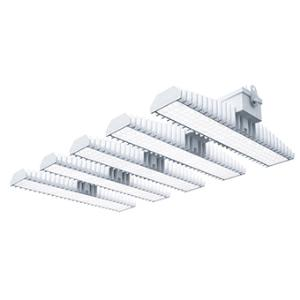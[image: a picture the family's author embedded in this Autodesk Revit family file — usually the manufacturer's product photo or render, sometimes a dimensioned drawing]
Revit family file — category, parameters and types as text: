
# Revit family: 3f_filippi_-_3f_lem_ht_ampio_3f_filippi_-_59030_a0812_-_3f_lem_5_ht_led_150_cr_ampio___vs_0ec2
name_source: partatom
category: Lighting Fixtures
units: mm (PartAtom-declared; Revit-internal decimal feet)

## family parameters
Cut with Voids When Loaded = No
Host = Face
Light Source = No
Part Type = Normal
Room Calculation Point = No
Round Connector Dimension = Use Diameter
Shared = No

## types (1)
- 3F Filippi - 3F LEM HT Ampio (1 x LED, 21295 lm, 170 W, 4000 K)
    Apparent Load = 170 VA
    Approval mark = ENEC
    CIE Flux Codes = 67 90 97 100 100
    Color Rendering = 80
    Color Temperature = 4000 K
    Control Gear = Electronic ballast
    Default Elevation = 1800 mm
    Description = Industrial luminaire with high light output and high luminous efficiency designed with the most innovative technologies for environments with temperature up to 70°C.

ILLUMINOTECHNICAL
Luminous efficiency 100% (DLOR 98%, ULOR 2%).
Initial luminous flux of the luminaire 21295 lm.
Direct symmetric wide distribution: the illuminated area has a rectangular shape.
Installation Interdistance Transv.D = 1.24 x hu - Long.D = 1.20 x hu.
Tabular UGR (CIE 117 - 4H-8H; S=0.25H; 70/50/20): RUG 21.3 - 21.3.
Beam angle: 82° - 83°.
Luminous efficacy 125 lm/W.
Lifetime (L93/B10): 30000 h. (tq+25°C)
Lifetime (L90/B10): 50000 h. (tq+25°C)
Lifetime (L85/B10): 80000 h. (tq+25°C)
Lifetime (L80/B10): 100000 h. (tq+25°C)
Lifetime (L85/B10): 50000 h. (tq+70°C)
Sudden decreased luminous flux after 50000 hours: 0% (C0).
Photobiological safety in compliance with IEC/TR 62778: RG0 risk exempt, (IEC 62471).
In compliance with IEC/EN 62722-2-1 - IEC/EN 62717 standards.
Luminous flux at +70°C: -13.5%.

SOURCE
5 Mid-Power linear LED modules 30W/840.
Energy efficiency class (UE 2019/2020 - UE 2019/2015): C.
CIE 13.3 Colour rendering index: CRI >80 (R9 <50%).
IES TM-30 Fidelity Index: Rf = 84 Rg = 95.
CCT nominal colour temperature 4000 K.
Colour initial tolerance (MacAdam): SDCM 3.

MECHANICAL
Passive modular heatsinks in die-casted aluminium, painted in white colour.
To optimize the thermal management of the LED module, the heatsinks are oversized and provided with self-cleaning of cooling fins.
Wiring body in aluminium and galvanised steel anchored solidly to the sinks and thermally separated.
3F Lens lenses with high luminous efficiency, transparent polycarbonate, fixed to the LED modules.
Fixing brackets in stainless steel.
Luminaire with limited surface temperature. - D - (EN 60598-2-24)
Dimensions: 952x542 mm, height 133 mm. Weight 23.78 kg.
IP65 protection degree.
Mechanical strength to impacts IK08 (5 joule).
Glow-wire test resistance 850°C.

ELECTRICAL
Halogen Free electronic wiring 230V-50/60Hz, power factor 0.95, THD <25%, constant output current, class I, 2 driver.
Power of the luminaire 170 W.
CE - IEC 60598-1 - EN 60598-1.
SAFE FLICKER: PstLM=<1 and SVM=<0.4 (IEC TR 61547-1 and IEC TR 63158), to ensure a more comfortable and safe light.
Luminaire compliant with EN 60598-2-22 for power supply from a centralised emergency system CPSS (Central Power Supply System), not incorporated in the luminaire - high risk areas excluded. The default power and flux are 100% in AC and 100% in DC.
Ambient temperature from -30°C to +70°C.
Temperature class T6 max 85°C.
Quick connection via M20 3P connector with 9-13 mm tightening range.
Power unit positioned on a separate compartment by the LED module to ensure optimum temperatures of cabling components, to be inspectable and maintainable.
Relative humidity UR: <85%.

INSTALLATION
Ceiling / Suspended / Wall.
All accessories dedicated to this product are available on the Catalog and on our website www.3F-Filippi.com.

ACCESSORIES
A0812 - Anti-glare microprismatic VS moulded glass, tempered, not flammable, with sealing gasket.
One required for each light module. The pack contains 10 pieces.

APPLICATIONS
In commercial environments, exhibition and industrial areas, stores, open areas.
Applications with high ambient temperature up to 70°C.

WARNING
Fixture not suitable for cold stores with an ambient temperature <0°C and/or relative humidity >85%.
Luminaire designed for disposal/recycling at end-of-life.
Replaceable (LED only) light source by a professional. Replaceable control gear by a professional.
    Height = 133 mm  [stored 0.436352 ft]
    Lamp = 1 x LED
    Lamp Light Flux = 21295 lm
    Lamp Power = 170 W
    Lamp count = 1
    Length = 952 mm
    Lifetime = 50000 h
    Luminous efficacy = 125 lm/W
    Manufacturer = 3F Filippi
    ModVariant = No
    Model = 3F Filippi - 59030+A0812 - 3F LEM 5 HT LED 150 CR AMPIO + VS
    Mounting Place = Ceiling
    Mounting Type = Pendant
    Number of Poles = 1
    OnlyDefault = Yes
    Power Factor = 1
    Product Name = 3F Filippi - 3F LEM HT Ampio
    Product group = pendant luminaire
    ProductGroupID = 9
    Protection Class = Protection class I
    Protection Degree = IP 65
    RLX_Detail_Level = 1
    RLX_Emergency_Light_Flux = 0 lm
    RLX_Emergency_Type = 0
    RLX_Emergency_Type_DB = No
    RlxData = <blob elided: 129133 chars, md5=752d8b28>
    Socket = socket
    Standby Power = 0 W
    System Light Flux = 21295 lm
    System Power = 170 W
    Type Comments = Product without accessories
    Type Image = 3f_filippi_-_lem_5__a0812.jpg
    URL = http://relux.com
    VarID = ---
    Voltage = 0 V
    Weight = 0.00 kg
    Width = 542 mm

note: [stored X ft] marks values corroborated as IEEE doubles in the binary element streams (Revit-internal decimal feet)

## geometry (parser evidence)
native form markers: Blend x4, Sweep x13
no freeform markers — native parametric forms only
